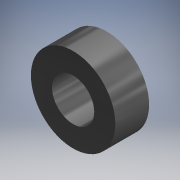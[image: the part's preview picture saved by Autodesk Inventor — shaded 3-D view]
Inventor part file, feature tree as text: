
AUTODESK INVENTOR PART (.ipt)
format: ipt  version: 2019 (Build 230136000, 136)  size: 90,112 bytes
history: native  units: mm (DEFAULTED — no unit token found)
features: extrude x1, sketch x1
ambient origin geometry x8: Origin, YZ Plane, XZ Plane, XY Plane, X Axis, Y Axis, Z Axis, Center Point
bodies: Solid1 (feature_tree)
feature tree (2):
  extrude  "Extrusion1"  Depth=5.08mm
  sketch  "Sketch1"  dims[d0=6.35mm d1=12.7mm d2=5.08mm d3=0.0mm]
